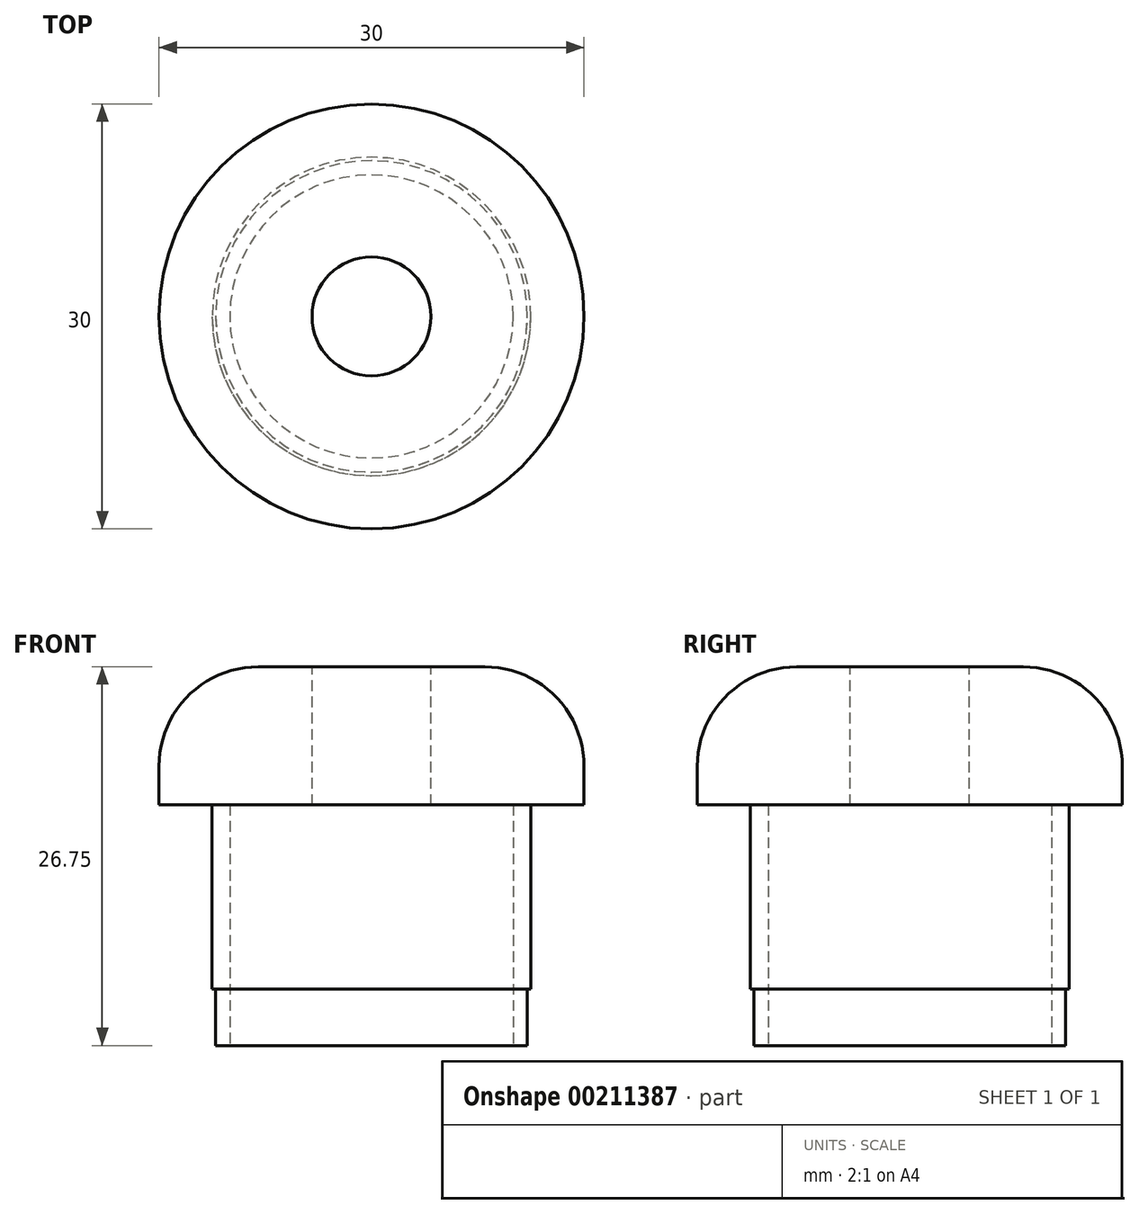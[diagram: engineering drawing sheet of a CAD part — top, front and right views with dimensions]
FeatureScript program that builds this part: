
annotation { "Feature Type Name" : "Feature", "Feature Type Description" : "" }
export const myFeature = defineFeature(function(context is Context, id is Id, definition is map)
    precondition{}
    {
        {
            var Q0;
            Q0=qCreatedBy(makeId("Top.planeOp"),FACE);
            var sketch = newSketch(context, id + "F0", { "sketchPlane" : qUnion([Q0])});
            skCircle(sketch, "E0", {"center": v(0, 0) * mm, "radius": 11 * mm});
            skCircle(sketch, "E1", {"center": v(0, 0) * mm, "radius": 10 * mm});
            skSolve(sketch);
        }
        {
            var Q0;
            Q0 = qSketchRegion(id + "F0", true);
            extrude(context, id + "F1", {"entities" : qUnion([Q0]), "depth" : 17 * mm});
        }
        {
            var Q0;
            Q0=makeQuery(id+"F1.opExtrude","CAP_FACE",FACE,{"disambiguationData":[OSD([sQuery(id+"F0.wireOp",EDGE,"E0"),sQuery(id+"F0.wireOp",EDGE,"E1")])],"isStart":false});
            var sketch = newSketch(context, id + "F2", { "sketchPlane" : qUnion([Q0])});
            skCircle(sketch, "E2", {"center": v(0, 0) * mm, "radius": 15 * mm});
            skSolve(sketch);
        }
        {
            var Q0;
            Q0 = qSketchRegion(id + "F2", true);
            extrude(context, id + "F3", {"entities" : qUnion([Q0]), "operationType" : NewBodyOperationType.ADD, "depth" : 9.75 * mm});
        }
        {
            var Q0;
            Q0=makeQuery(id+"F3.opExtrude","CAP_EDGE",EDGE,{"disambiguationData":[OSD([sQuery(id+"F2.wireOp",EDGE,"E2")])],"isStart":false});
            fillet(context, id + "F4", {"entities" : qUnion([Q0]), "radius" : 7 * mm, "tangentPropagation" : true, "allowEdgeOverflow" : false});
        }
        {
            var Q0;
            Q0=makeQuery(id+"F1.opExtrude","CAP_FACE",FACE,{"disambiguationData":[OSD([sQuery(id+"F0.wireOp",EDGE,"E0"),sQuery(id+"F0.wireOp",EDGE,"E1")])],"isStart":true});
            cPlane(context, id + "F5", {"entities" : qUnion([Q0]), "cplaneType" : CPlaneType.OFFSET, "offset" : 4 * mm, "oppositeDirection" : true, "width" : 152.4 * mm, "height" : 152.4 * mm});
        }
        {
            var Q0;
            Q0=qCreatedBy(id+"F5.planeOp",FACE);
            var sketch = newSketch(context, id + "F6", { "sketchPlane" : qUnion([Q0])});
            skCircle(sketch, "E3", {"center": v(0, 0) * mm, "radius": 11.25 * mm});
            skCircle(sketch, "E4.0", {"center": v(0, 0) * mm, "radius": 11 * mm});
            skSolve(sketch);
        }
        {
            var Q0;
            Q0 = qSketchRegion(id + "F6", true);
            var Q1;
            {var subQ0=sQuery(id+"F2.wireOp",EDGE,"E2");Q1=makeQuery(id+"F3.boolean.opBoolean","SPLIT",FACE,{"disambiguationData":[TD([makeQuery(id+"F1.opExtrude","SWEPT_FACE",FACE,{"disambiguationData":[OSD([sQuery(id+"F0.wireOp",EDGE,"E0")])]})])],"derivedFrom":makeQuery(id+"F3.opExtrude","CAP_FACE",FACE,{"disambiguationData":[OSD([subQ0])],"isStart":true})});}
            extrude(context, id + "F7", {"entities" : qUnion([Q0]), "operationType" : NewBodyOperationType.ADD, "endBound" : BoundingType.UP_TO_SURFACE, "oppositeDirection" : true, "endBoundEntityFace" : qUnion([Q1]), "depth" : 10 * mm});
        }
        {
            var Q0;
            Q0=makeQuery(id+"F3.opExtrude","CAP_FACE",FACE,{"disambiguationData":[OSD([sQuery(id+"F2.wireOp",EDGE,"E2")])],"isStart":false});
            var sketch = newSketch(context, id + "F8", { "sketchPlane" : qUnion([Q0])});
            skCircle(sketch, "E5", {"center": v(0, 0) * mm, "radius": 4.2 * mm});
            skSolve(sketch);
        }
        {
            var Q0;
            Q0 = qSketchRegion(id + "F8", true);
            extrude(context, id + "F9", {"entities" : qUnion([Q0]), "operationType" : NewBodyOperationType.REMOVE, "oppositeDirection" : true, "depth" : 25.4 * mm});
        }
    });
